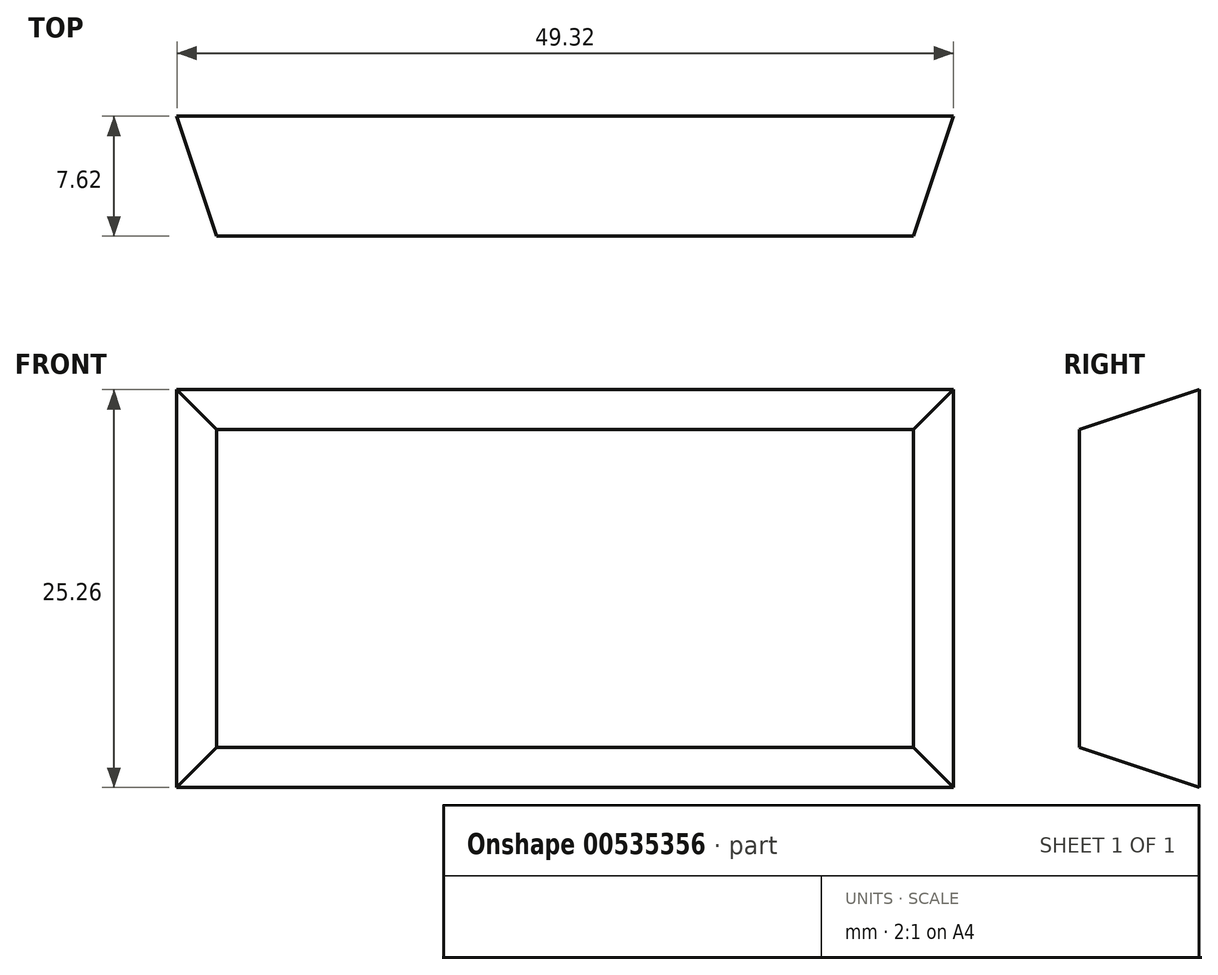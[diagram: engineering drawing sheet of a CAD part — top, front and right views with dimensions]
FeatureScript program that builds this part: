
annotation { "Feature Type Name" : "Feature", "Feature Type Description" : "" }
export const myFeature = defineFeature(function(context is Context, id is Id, definition is map)
    precondition{}
    {
        {
            var Q0;
            Q0=qCreatedBy(makeId("Front.planeOp"),FACE);
            var sketch = newSketch(context, id + "F0", { "sketchPlane" : qUnion([Q0])});
            skLineSegment(sketch, "E0.bottom", {"start": v(24.66, -12.63) * mm, "end": v(-24.66, -12.63) * mm});
            skLineSegment(sketch, "E0.top", {"start": v(24.66, 12.63) * mm, "end": v(-24.66, 12.63) * mm});
            skLineSegment(sketch, "E0.left", {"start": v(24.66, -12.63) * mm, "end": v(24.66, 12.63) * mm});
            skLineSegment(sketch, "E0.right", {"start": v(-24.66, -12.63) * mm, "end": v(-24.66, 12.63) * mm});
            skPoint(sketch, "E0.middle", {"position": v(0, 0) * mm});
            skSolve(sketch);
        }
        {
            var Q0;
            Q0=makeQuery(id+"F0.imprint","IMPRINT",FACE,{"disambiguationData":[TD([[makeQuery(id+"F0.imprint","IMPRINT",EDGE,{"derivedFrom":sQuery(id+"F0.wireOp",EDGE,"E0.bottom")}),-1.0]])]});
            extrude(context, id + "F1", {"entities" : qUnion([Q0]), "depth" : 7.62 * mm, "offsetDistance" : 25.4 * mm});
        }
        {
            var Q0;
            Q0=makeQuery(id+"F1.opExtrude","CAP_EDGE",EDGE,{"disambiguationData":[OSD([sQuery(id+"F0.wireOp",EDGE,"E0.top")])],"isStart":false});
            var Q1;
            Q1=makeQuery(id+"F1.opExtrude","CAP_EDGE",EDGE,{"disambiguationData":[OSD([sQuery(id+"F0.wireOp",EDGE,"E0.left")])],"isStart":false});
            var Q2;
            Q2=makeQuery(id+"F1.opExtrude","CAP_EDGE",EDGE,{"disambiguationData":[OSD([sQuery(id+"F0.wireOp",EDGE,"E0.right")])],"isStart":false});
            var Q3;
            Q3=makeQuery(id+"F1.opExtrude","CAP_EDGE",EDGE,{"disambiguationData":[OSD([sQuery(id+"F0.wireOp",EDGE,"E0.bottom")])],"isStart":false});
            chamfer(context, id + "F2", {"entities" : qUnion([Q0, Q1, Q2, Q3]), "chamferType" : ChamferType.TWO_OFFSETS, "width1" : 2.54 * mm, "oppositeDirection" : false, "width2" : 7.62 * mm, "tangentPropagation" : true});
        }
    });
